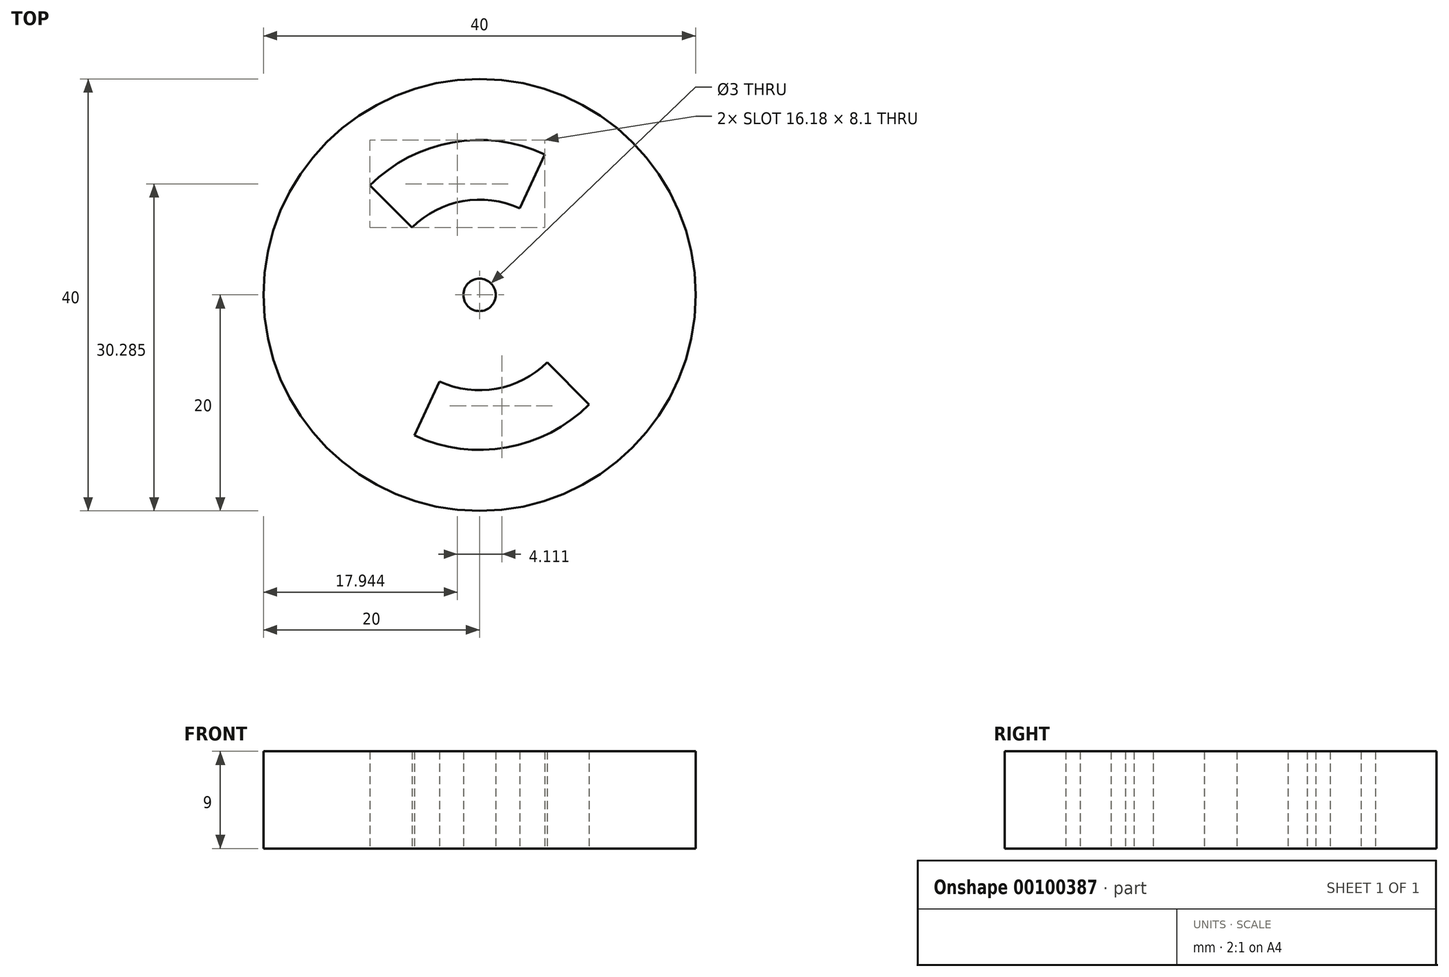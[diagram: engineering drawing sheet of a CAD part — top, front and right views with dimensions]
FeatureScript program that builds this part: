
annotation { "Feature Type Name" : "Feature", "Feature Type Description" : "" }
export const myFeature = defineFeature(function(context is Context, id is Id, definition is map)
    precondition{}
    {
        {
            var Q0;
            Q0=qCreatedBy(makeId("Top.planeOp"),FACE);
            var sketch = newSketch(context, id + "F0", { "sketchPlane" : qUnion([Q0])});
            skCircle(sketch, "E0", {"center": v(0, 0) * mm, "radius": 20 * mm});
            skCircle(sketch, "E1", {"center": v(0, 0) * mm, "radius": 1.5 * mm});
            skArc(sketch, "E2", {"start": v(-3.71, -8) * mm, "mid": v(1.54, -8.69) * mm, "end": v(6.24, -6.23) * mm});
            skArc(sketch, "E3", {"start": v(-6.04, -13) * mm, "mid": v(2.5, -14.12) * mm, "end": v(10.15, -10.13) * mm});
            skLineSegment(sketch, "E4", {"start": v(-6.24, 6.23) * mm, "end": v(-10.15, 10.13) * mm});
            skLineSegment(sketch, "E5", {"start": v(-10.15, 10.13) * mm, "end": v(-6.24, 6.23) * mm});
            skLineSegment(sketch, "E6", {"start": v(10.15, -10.13) * mm, "end": v(6.24, -6.23) * mm});
            skLineSegment(sketch, "E7", {"start": v(0.63, 1.36) * mm, "end": v(6.04, 13) * mm});
            skLineSegment(sketch, "E8", {"start": v(6.04, 13) * mm, "end": v(3.71, 8) * mm});
            skLineSegment(sketch, "E9", {"start": v(-6.04, -13) * mm, "end": v(-3.71, -8) * mm});
            skArc(sketch, "E10.trimOffspring", {"start": v(3.71, 8) * mm, "mid": v(-1.54, 8.69) * mm, "end": v(-6.24, 6.23) * mm});
            skArc(sketch, "E11.trimOffspring", {"start": v(6.04, 13) * mm, "mid": v(-2.5, 14.12) * mm, "end": v(-10.15, 10.13) * mm});
            skLineSegment(sketch, "E12.trimOffspring", {"start": v(-3.71, -8) * mm, "end": v(-6.04, -13) * mm});
            skLineSegment(sketch, "E13.trimOffspring", {"start": v(6.24, -6.23) * mm, "end": v(10.15, -10.13) * mm});
            skSolve(sketch);
        }
        {
            var Q0;
            Q0=makeQuery(id+"F0.imprint","IMPRINT",FACE,{"disambiguationData":[TD([[makeQuery(id+"F0.imprint","IMPRINT",EDGE,{"derivedFrom":sQuery(id+"F0.wireOp",EDGE,"E0")}),1.0]])]});
            var Q1;
            {var subQ5=sQuery(id+"F0.wireOp",EDGE,"sUIQ6igV-4INL-CtkN-Za45-nuTRUdYhnrlg.top");Q1=makeQuery(id+"F0.imprint","IMPRINT",FACE,{"disambiguationData":[TD([[makeQuery(id+"F0.imprint","IMPRINT",EDGE,{"derivedFrom":subQ5}),-1.0]])]});}
            extrude(context, id + "F1", {"entities" : qUnion([Q0, Q1]), "depth" : 9 * mm});
        }
    });
